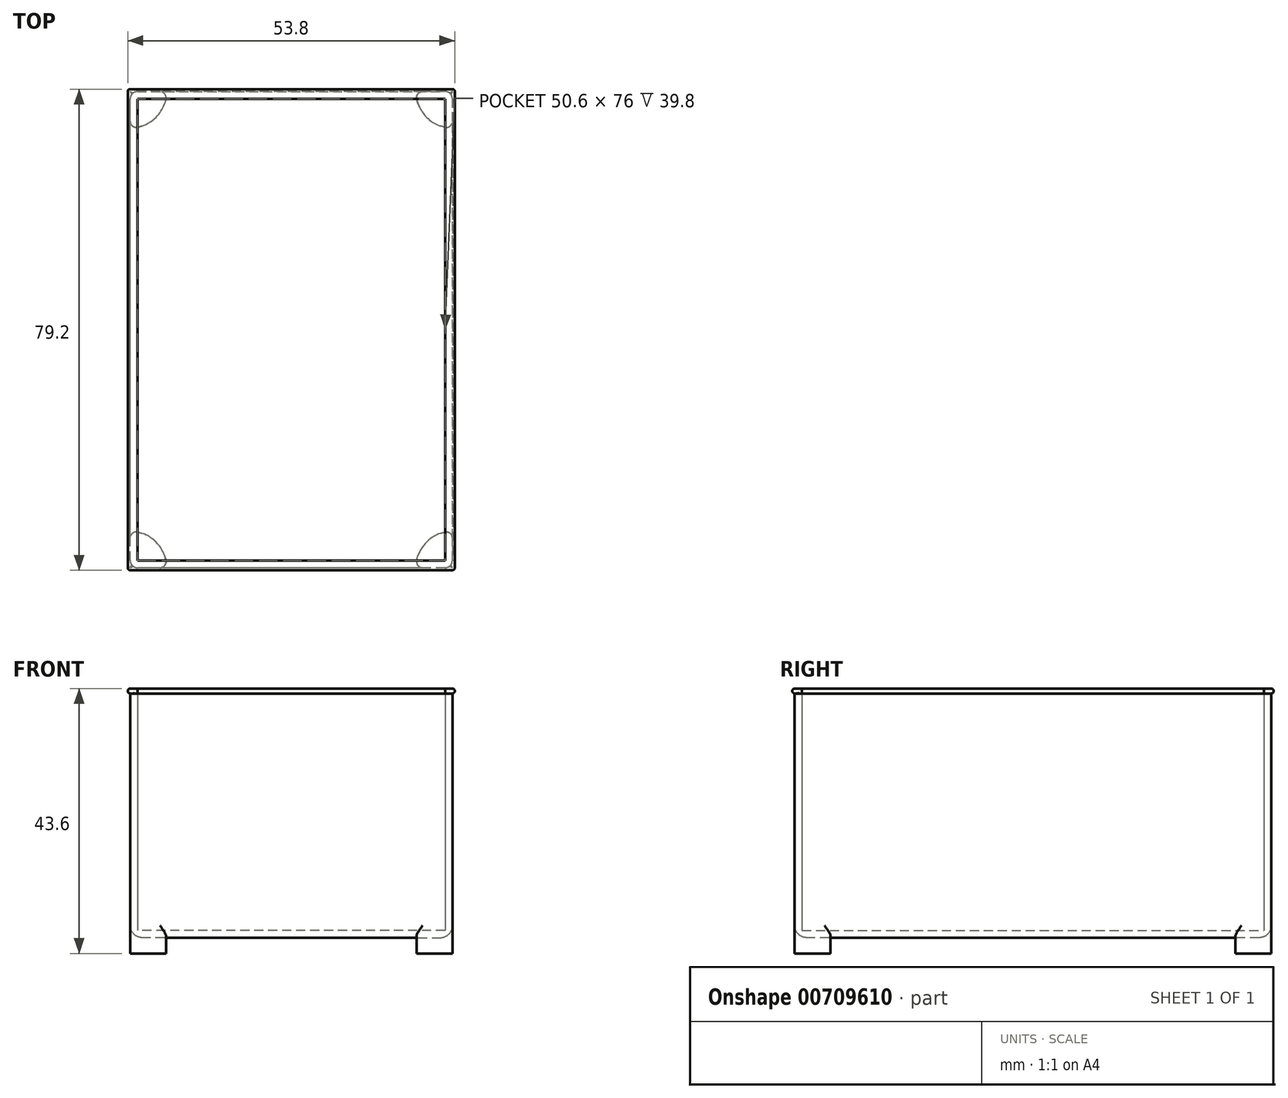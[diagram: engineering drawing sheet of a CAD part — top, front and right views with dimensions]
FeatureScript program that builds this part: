
annotation { "Feature Type Name" : "Feature", "Feature Type Description" : "" }
export const myFeature = defineFeature(function(context is Context, id is Id, definition is map)
    precondition{}
    {
        {
            var Q0;
            Q0=qCreatedBy(makeId("Front.planeOp"),FACE);
            var sketch = newSketch(context, id + "F0", { "sketchPlane" : qUnion([Q0])});
            skLineSegment(sketch, "E0.bottom", {"start": v(26.5, 20.5) * mm, "end": v(-26.5, 20.5) * mm});
            skLineSegment(sketch, "E0.top", {"start": v(26.5, -20.5) * mm, "end": v(-26.5, -20.5) * mm});
            skLineSegment(sketch, "E0.left", {"start": v(26.5, 20.5) * mm, "end": v(26.5, -20.5) * mm});
            skLineSegment(sketch, "E0.right", {"start": v(-26.5, 20.5) * mm, "end": v(-26.5, -20.5) * mm});
            skPoint(sketch, "E0.middle", {"position": v(0, 0) * mm});
            skSolve(sketch);
        }
        {
            var Q0;
            Q0=makeQuery(id+"F0.imprint","IMPRINT",FACE,{"disambiguationData":[TD([[makeQuery(id+"F0.imprint","IMPRINT",EDGE,{"derivedFrom":sQuery(id+"F0.wireOp",EDGE,"E0.bottom")}),1.0]])]});
            extrude(context, id + "F1", {"entities" : qUnion([Q0]), "depth" : 78.4 * mm, "offsetDistance" : 25 * mm, "symmetric" : true});
        }
        {
            var Q0;
            Q0=makeQuery(id+"F1.opExtrude","SWEPT_FACE",FACE,{"disambiguationData":[OSD([sQuery(id+"F0.wireOp",EDGE,"E0.bottom")])]});
            shell(context, id + "F2", {"entities" : qUnion([Q0]), "thickness" : 1.2 * mm});
        }
        {
            var Q0;
            Q0=makeQuery(id+"F1.opExtrude","SWEPT_FACE",FACE,{"disambiguationData":[OSD([sQuery(id+"F0.wireOp",EDGE,"E0.top")])]});
            var sketch = newSketch(context, id + "F3", { "sketchPlane" : qUnion([Q0])});
            skArc(sketch, "E1", {"start": v(20.62, 38) * mm, "mid": v(22.26, 34.96) * mm, "end": v(25.3, 33.32) * mm});
            skLineSegment(sketch, "E2", {"start": v(26.5, 39.2) * mm, "end": v(21.6, 39.2) * mm});
            skLineSegment(sketch, "E3", {"start": v(26.5, 39.2) * mm, "end": v(26.5, 34.3) * mm});
            skPoint(sketch, "E4.visualSharp", {"position": v(20.5, 39.2) * mm});
            skArc(sketch, "E4.filletArc", {"start": v(21.6, 39.2) * mm, "mid": v(20.83, 38.83) * mm, "end": v(20.62, 38) * mm});
            skPoint(sketch, "E5.visualSharp", {"position": v(26.5, 33.2) * mm});
            skArc(sketch, "E5.filletArc", {"start": v(25.3, 33.32) * mm, "mid": v(26.13, 33.53) * mm, "end": v(26.5, 34.3) * mm});
            skArc(sketch, "E6.MirrorCS", {"start": v(-25.3, 33.32) * mm, "mid": v(-26.13, 33.53) * mm, "end": v(-26.5, 34.3) * mm});
            skArc(sketch, "E7.MirrorCS", {"start": v(-21.6, 39.2) * mm, "mid": v(-20.83, 38.83) * mm, "end": v(-20.62, 38) * mm});
            skPoint(sketch, "E8.MirrorP", {"position": v(-20.5, 39.2) * mm});
            skArc(sketch, "E9.MirrorCS", {"start": v(-20.62, 38) * mm, "mid": v(-22.26, 34.96) * mm, "end": v(-25.3, 33.32) * mm});
            skLineSegment(sketch, "E10.MirrorCS", {"start": v(-26.5, 39.2) * mm, "end": v(-21.6, 39.2) * mm});
            skLineSegment(sketch, "E11.MirrorCS", {"start": v(-26.5, 39.2) * mm, "end": v(-26.5, 34.3) * mm});
            skPoint(sketch, "E12.MirrorP", {"position": v(-26.5, 33.2) * mm});
            skArc(sketch, "E13.MirrorCS", {"start": v(25.3, -33.32) * mm, "mid": v(26.13, -33.53) * mm, "end": v(26.5, -34.3) * mm});
            skArc(sketch, "E14.MirrorCS", {"start": v(21.6, -39.2) * mm, "mid": v(20.83, -38.83) * mm, "end": v(20.62, -38) * mm});
            skArc(sketch, "E15.MirrorCS", {"start": v(-25.3, -33.32) * mm, "mid": v(-26.13, -33.53) * mm, "end": v(-26.5, -34.3) * mm});
            skArc(sketch, "E16.MirrorCS", {"start": v(-21.6, -39.2) * mm, "mid": v(-20.83, -38.83) * mm, "end": v(-20.62, -38) * mm});
            skPoint(sketch, "E17.MirrorP", {"position": v(-26.5, -33.2) * mm});
            skPoint(sketch, "E18.MirrorP", {"position": v(20.5, -39.2) * mm});
            skPoint(sketch, "E19.MirrorP", {"position": v(26.5, -33.2) * mm});
            skLineSegment(sketch, "E20.MirrorCS", {"start": v(-26.5, -39.2) * mm, "end": v(-26.5, -34.3) * mm});
            skPoint(sketch, "E21.MirrorP", {"position": v(-20.5, -39.2) * mm});
            skLineSegment(sketch, "E22.MirrorCS", {"start": v(26.5, -39.2) * mm, "end": v(26.5, -34.3) * mm});
            skLineSegment(sketch, "E23.MirrorCS", {"start": v(-26.5, -39.2) * mm, "end": v(-21.6, -39.2) * mm});
            skLineSegment(sketch, "E24.MirrorCS", {"start": v(26.5, -39.2) * mm, "end": v(21.6, -39.2) * mm});
            skArc(sketch, "E25.MirrorCS", {"start": v(20.62, -38) * mm, "mid": v(22.26, -34.96) * mm, "end": v(25.3, -33.32) * mm});
            skArc(sketch, "E26.MirrorCS", {"start": v(-20.62, -38) * mm, "mid": v(-22.26, -34.96) * mm, "end": v(-25.3, -33.32) * mm});
            skSolve(sketch);
        }
        {
            var Q0;
            Q0 = qSketchRegion(id + "F3", true);
            extrude(context, id + "F4", {"entities" : qUnion([Q0]), "operationType" : NewBodyOperationType.ADD, "depth" : 2.6 * mm, "offsetDistance" : 25 * mm});
        }
        {
            var Q0;
            Q0=makeQuery(id+"F4.boolean.opBoolean","MERGE",FACE,{"derivedFrom":[makeQuery(id+"F1.opExtrude","CAP_FACE",FACE,{"disambiguationData":[OSD([sQuery(id+"F0.wireOp",EDGE,"E0.bottom"),sQuery(id+"F0.wireOp",EDGE,"E0.top"),sQuery(id+"F0.wireOp",EDGE,"E0.left"),sQuery(id+"F0.wireOp",EDGE,"E0.right")])],"isStart":false}),makeQuery(id+"F4.opExtrude","SWEPT_FACE",FACE,{"disambiguationData":[OSD([sQuery(id+"F3.wireOp",EDGE,"E2")])]}),makeQuery(id+"F4.opExtrude","SWEPT_FACE",FACE,{"disambiguationData":[OSD([sQuery(id+"F3.wireOp",EDGE,"E10.MirrorCS")])]})]});
            var sketch = newSketch(context, id + "F5", { "sketchPlane" : qUnion([Q0])});
            skLineSegment(sketch, "E27", {"start": v(-26.5, 20.5) * mm, "end": v(-26.5, 19.7) * mm});
            skArc(sketch, "E28", {"start": v(-26.5, 20.5) * mm, "mid": v(-26.9, 20.1) * mm, "end": v(-26.5, 19.7) * mm});
            skSolve(sketch);
        }
        {
            var Q0;
            Q0=makeQuery(id+"F5.imprint","IMPRINT",FACE,{"disambiguationData":[TD([[makeQuery(id+"F5.imprint","IMPRINT",EDGE,{"derivedFrom":sQuery(id+"F5.wireOp",EDGE,"E27")}),-1.0]])]});
            var Q1;
            Q1=makeQuery(id+"F1.opExtrude","SWEPT_EDGE",EDGE,{"disambiguationData":[OSD([sQuery(id+"F0.wireOp",EDGE,"E0.bottom"),sQuery(id+"F0.wireOp",EDGE,"E0.right")])]});
            var Q2;
            Q2=makeQuery(id+"F1.opExtrude","CAP_EDGE",EDGE,{"disambiguationData":[OSD([sQuery(id+"F0.wireOp",EDGE,"E0.bottom")])],"isStart":false});
            var Q3;
            Q3=makeQuery(id+"F1.opExtrude","SWEPT_EDGE",EDGE,{"disambiguationData":[OSD([sQuery(id+"F0.wireOp",EDGE,"E0.bottom"),sQuery(id+"F0.wireOp",EDGE,"E0.left")])]});
            var Q4;
            Q4=makeQuery(id+"F1.opExtrude","CAP_EDGE",EDGE,{"disambiguationData":[OSD([sQuery(id+"F0.wireOp",EDGE,"E0.bottom")])],"isStart":true});
            sweep(context, id + "F6", {"operationType" : NewBodyOperationType.ADD, "profiles" : qUnion([Q0]), "path" : qUnion([Q1, Q2, Q3, Q4])});
        }
        {
            var Q0;
            Q0=makeQuery(id+"F1.opExtrude","CAP_EDGE",EDGE,{"disambiguationData":[OSD([sQuery(id+"F0.wireOp",EDGE,"E0.top")])],"isStart":false});
            var Q1;
            Q1=makeQuery(id+"F1.opExtrude","SWEPT_EDGE",EDGE,{"disambiguationData":[OSD([sQuery(id+"F0.wireOp",EDGE,"E0.top"),sQuery(id+"F0.wireOp",EDGE,"E0.left")])]});
            var Q2;
            Q2=makeQuery(id+"F1.opExtrude","SWEPT_EDGE",EDGE,{"disambiguationData":[OSD([sQuery(id+"F0.wireOp",EDGE,"E0.top"),sQuery(id+"F0.wireOp",EDGE,"E0.right")])]});
            var Q3;
            Q3=makeQuery(id+"F1.opExtrude","CAP_EDGE",EDGE,{"disambiguationData":[OSD([sQuery(id+"F0.wireOp",EDGE,"E0.top")])],"isStart":true});
            fillet(context, id + "F7", {"entities" : qUnion([Q0, Q1, Q2, Q3]), "radius" : 2 * mm, "tangentPropagation" : true, "allowEdgeOverflow" : false});
        }
        {
            var Q0;
            Q0=makeQuery(id+"F4.boolean.opBoolean","MERGE",EDGE,{"derivedFrom":[makeQuery(id+"F1.opExtrude","CAP_EDGE",EDGE,{"disambiguationData":[OSD([sQuery(id+"F0.wireOp",EDGE,"E0.right")])],"isStart":false}),makeQuery(id+"F4.opExtrude","SWEPT_EDGE",EDGE,{"disambiguationData":[OSD([sQuery(id+"F3.wireOp",EDGE,"E10.MirrorCS"),sQuery(id+"F3.wireOp",EDGE,"E11.MirrorCS")])]})]});
            var Q1;
            Q1=makeQuery(id+"F4.boolean.opBoolean","MERGE",EDGE,{"derivedFrom":[makeQuery(id+"F1.opExtrude","CAP_EDGE",EDGE,{"disambiguationData":[OSD([sQuery(id+"F0.wireOp",EDGE,"E0.left")])],"isStart":false}),makeQuery(id+"F4.opExtrude","SWEPT_EDGE",EDGE,{"disambiguationData":[OSD([sQuery(id+"F3.wireOp",EDGE,"E2"),sQuery(id+"F3.wireOp",EDGE,"E3")])]})]});
            var Q2;
            Q2=makeQuery(id+"F4.boolean.opBoolean","MERGE",EDGE,{"derivedFrom":[makeQuery(id+"F1.opExtrude","CAP_EDGE",EDGE,{"disambiguationData":[OSD([sQuery(id+"F0.wireOp",EDGE,"E0.left")])],"isStart":true}),makeQuery(id+"F4.opExtrude","SWEPT_EDGE",EDGE,{"disambiguationData":[OSD([sQuery(id+"F3.wireOp",EDGE,"E22.MirrorCS"),sQuery(id+"F3.wireOp",EDGE,"E24.MirrorCS")])]})]});
            var Q3;
            Q3=makeQuery(id+"F4.boolean.opBoolean","MERGE",EDGE,{"derivedFrom":[makeQuery(id+"F1.opExtrude","CAP_EDGE",EDGE,{"disambiguationData":[OSD([sQuery(id+"F0.wireOp",EDGE,"E0.right")])],"isStart":true}),makeQuery(id+"F4.opExtrude","SWEPT_EDGE",EDGE,{"disambiguationData":[OSD([sQuery(id+"F3.wireOp",EDGE,"E20.MirrorCS"),sQuery(id+"F3.wireOp",EDGE,"E23.MirrorCS")])]})]});
            fillet(context, id + "F8", {"entities" : qUnion([Q0, Q1, Q2, Q3]), "radius" : 1.2 * mm, "tangentPropagation" : true, "allowEdgeOverflow" : false});
        }
        {
            var Q0;
            Q0=makeQuery(id+"F6.opSweep","MID_CAP_EDGE",EDGE,{"disambiguationData":[OSD([sQuery(id+"F0.wireOp",EDGE,"E0.bottom"),sQuery(id+"F0.wireOp",EDGE,"E0.right"),sQuery(id+"F5.wireOp",EDGE,"E28")])],"capPos":1.0});
            var Q1;
            Q1=makeQuery(id+"F6.opSweep","CAP_EDGE",EDGE,{"disambiguationData":[OSD([sQuery(id+"F0.wireOp",EDGE,"E0.bottom"),sQuery(id+"F0.wireOp",EDGE,"E0.right"),sQuery(id+"F5.wireOp",EDGE,"E28")])],"isStart":true});
            var Q2;
            Q2=makeQuery(id+"F6.opSweep","MID_CAP_EDGE",EDGE,{"disambiguationData":[OSD([sQuery(id+"F0.wireOp",EDGE,"E0.bottom"),sQuery(id+"F0.wireOp",EDGE,"E0.left"),sQuery(id+"F5.wireOp",EDGE,"E28")])],"capPos":3.0});
            var Q3;
            Q3=makeQuery(id+"F6.opSweep","MID_CAP_EDGE",EDGE,{"disambiguationData":[OSD([sQuery(id+"F0.wireOp",EDGE,"E0.bottom"),sQuery(id+"F0.wireOp",EDGE,"E0.left"),sQuery(id+"F5.wireOp",EDGE,"E28")])],"capPos":2.0});
            fillet(context, id + "F9", {"entities" : qUnion([Q0, Q1, Q2, Q3]), "radius" : .4 * mm, "tangentPropagation" : true, "allowEdgeOverflow" : false});
        }
    });
